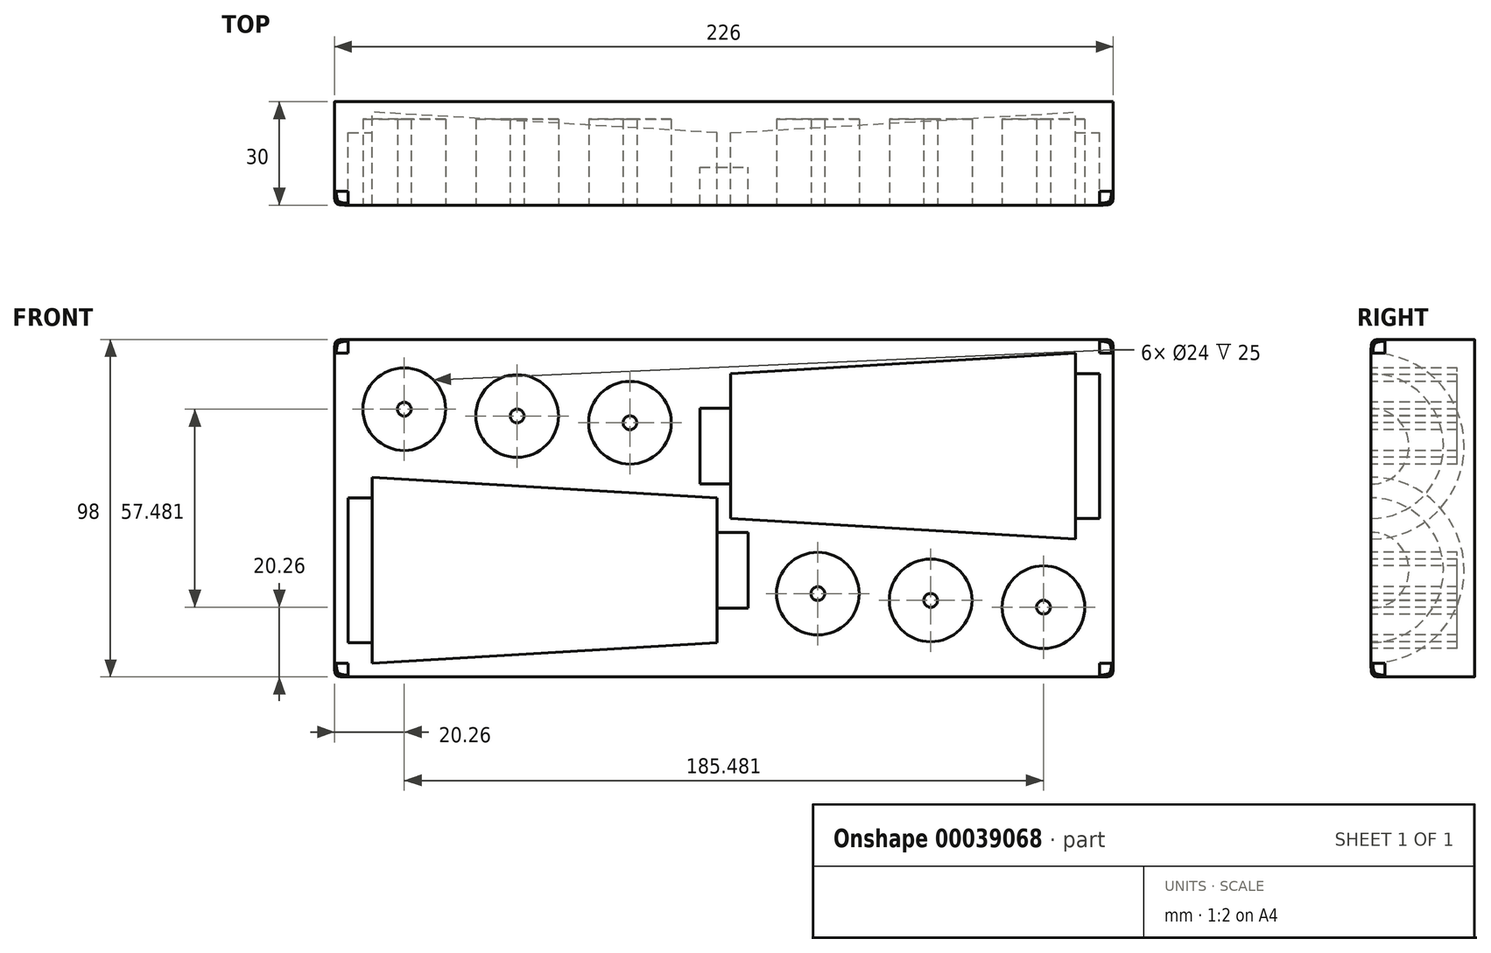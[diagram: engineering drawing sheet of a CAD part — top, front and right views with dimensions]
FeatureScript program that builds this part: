
annotation { "Feature Type Name" : "Feature", "Feature Type Description" : "" }
export const myFeature = defineFeature(function(context is Context, id is Id, definition is map)
    precondition{}
    {
        {
            var Q0;
            Q0=qCreatedBy(makeId("Front.planeOp"),FACE);
            var sketch = newSketch(context, id + "F0", { "sketchPlane" : qUnion([Q0])});
            skLineSegment(sketch, "E0.rect.bottom", {"start": v(-113, -49) * mm, "end": v(113, -49) * mm});
            skLineSegment(sketch, "E0.rect.top", {"start": v(-113, 49) * mm, "end": v(113, 49) * mm});
            skLineSegment(sketch, "E0.rect.left", {"start": v(-113, -49) * mm, "end": v(-113, 49) * mm});
            skLineSegment(sketch, "E0.rect.right", {"start": v(113, -49) * mm, "end": v(113, 49) * mm});
            skPoint(sketch, "E0.rect.middle", {"position": v(0, 0) * mm});
            skLineSegment(sketch, "E1", {"start": v(102, 45) * mm, "end": v(102, 39) * mm, "construction": true});
            skLineSegment(sketch, "E2", {"start": v(102, 39) * mm, "end": v(109, 39) * mm, "construction": true});
            skLineSegment(sketch, "E3", {"start": v(109, 18) * mm, "end": v(109, -3) * mm});
            skLineSegment(sketch, "E4", {"start": v(109, -3) * mm, "end": v(102, -3) * mm});
            skLineSegment(sketch, "E5", {"start": v(102, -3) * mm, "end": v(102, -9) * mm});
            skLineSegment(sketch, "E6", {"start": v(102, -9) * mm, "end": v(2, -3) * mm});
            skLineSegment(sketch, "E7", {"start": v(2, -3) * mm, "end": v(2, 7) * mm});
            skLineSegment(sketch, "E8", {"start": v(2, 7) * mm, "end": v(-7, 7) * mm});
            skLineSegment(sketch, "E9", {"start": v(-7, 7) * mm, "end": v(-7, 18) * mm});
            skLineSegment(sketch, "E10", {"start": v(-7, 29) * mm, "end": v(2, 29) * mm, "construction": true});
            skLineSegment(sketch, "E11", {"start": v(2, 29) * mm, "end": v(2, 39) * mm, "construction": true});
            skLineSegment(sketch, "E12", {"start": v(2, 39) * mm, "end": v(102, 45) * mm, "construction": true});
            skLineSegment(sketch, "E13", {"start": v(-7, 18) * mm, "end": v(109, 18) * mm});
            skLineSegment(sketch, "E14", {"start": v(51.88, -8) * mm, "end": v(113, -11.66) * mm, "construction": true});
            skLineSegment(sketch, "E15", {"start": v(52, -6) * mm, "end": v(51.88, -8) * mm, "construction": true});
            skLineSegment(sketch, "E16", {"start": v(-102, 9) * mm, "end": v(-2, 3) * mm, "construction": true});
            skLineSegment(sketch, "E17", {"start": v(-2, 3) * mm, "end": v(-2, -7) * mm, "construction": true});
            skLineSegment(sketch, "E18", {"start": v(-2, -7) * mm, "end": v(7, -7) * mm, "construction": true});
            skLineSegment(sketch, "E19", {"start": v(7, -18) * mm, "end": v(7, -29) * mm});
            skLineSegment(sketch, "E20", {"start": v(7, -29) * mm, "end": v(-2, -29) * mm});
            skLineSegment(sketch, "E21", {"start": v(-2, -29) * mm, "end": v(-2, -39) * mm});
            skLineSegment(sketch, "E22", {"start": v(-2, -39) * mm, "end": v(-102, -45) * mm});
            skLineSegment(sketch, "E23", {"start": v(-102, -45) * mm, "end": v(-102, -39) * mm});
            skLineSegment(sketch, "E24", {"start": v(-102, -39) * mm, "end": v(-109, -39) * mm});
            skLineSegment(sketch, "E25", {"start": v(-109, -39) * mm, "end": v(-109, -18) * mm});
            skLineSegment(sketch, "E26", {"start": v(-109, 3) * mm, "end": v(-102, 3) * mm, "construction": true});
            skLineSegment(sketch, "E27", {"start": v(-102, 3) * mm, "end": v(-102, 9) * mm, "construction": true});
            skLineSegment(sketch, "E28", {"start": v(-109, -18) * mm, "end": v(7, -18) * mm});
            skPoint(sketch, "E29.rect.middle", {"position": v(-57.95, 29) * mm});
            skPoint(sketch, "E30.rect.middle", {"position": v(57.95, -29) * mm});
            skLineSegment(sketch, "E31", {"start": v(-109, 3) * mm, "end": v(-109, -18) * mm, "construction": true});
            skLineSegment(sketch, "E32", {"start": v(-7, 29) * mm, "end": v(-7, 18) * mm, "construction": true});
            skLineSegment(sketch, "E33", {"start": v(109, 39) * mm, "end": v(109, 18) * mm, "construction": true});
            skLineSegment(sketch, "E34", {"start": v(7, -7) * mm, "end": v(7, -18) * mm, "construction": true});
            skPoint(sketch, "E35.start.orphan", {"position": v(-31.95, 41) * mm});
            skPoint(sketch, "E29.rect.left.end.orphan", {"position": v(-31.95, 29) * mm});
            skPoint(sketch, "E29.rect.bottom.start.orphan", {"position": v(-31.95, 17) * mm});
            skPoint(sketch, "E29.rect.right.start.orphan", {"position": v(-83.95, 17) * mm});
            skPoint(sketch, "E36.start.orphan", {"position": v(-83.95, 41) * mm});
            skPoint(sketch, "E37.start.orphan", {"position": v(-83.95, 29) * mm});
            skPoint(sketch, "E38.end.orphan", {"position": v(31.95, -29) * mm});
            skPoint(sketch, "E30.rect.bottom.end.orphan", {"position": v(31.95, -17) * mm});
            skPoint(sketch, "E39.start.orphan", {"position": v(83.95, -17) * mm});
            skPoint(sketch, "E40.end.orphan", {"position": v(83.95, -29) * mm});
            skPoint(sketch, "E30.rect.top.end.orphan", {"position": v(31.95, -41) * mm});
            skPoint(sketch, "E30.rect.top.start.orphan", {"position": v(83.95, -41) * mm});
            skLineSegment(sketch, "E41", {"start": v(-92.74, 28.74) * mm, "end": v(-27.26, 24.81) * mm, "construction": true});
            skCircle(sketch, "E42", {"center": v(-92.74, 28.74) * mm, "radius": 12 * mm});
            skCircle(sketch, "E43", {"center": v(-60, 26.78) * mm, "radius": 12 * mm});
            skCircle(sketch, "E44", {"center": v(-27.26, 24.81) * mm, "radius": 12 * mm});
            skLineSegment(sketch, "E45", {"start": v(-104.74, 28.74) * mm, "end": v(-113, 28.74) * mm, "construction": true});
            skLineSegment(sketch, "E46", {"start": v(-92.74, 40.74) * mm, "end": v(-92.74, 49) * mm, "construction": true});
            skLineSegment(sketch, "E47", {"start": v(-15.26, 24.81) * mm, "end": v(-7, 24.81) * mm, "construction": true});
            skLineSegment(sketch, "E48", {"start": v(-60.72, 14.8) * mm, "end": v(-61.21, 6.55) * mm, "construction": true});
            skLineSegment(sketch, "E49", {"start": v(27.26, -24.81) * mm, "end": v(92.74, -28.74) * mm, "construction": true});
            skCircle(sketch, "E50", {"center": v(92.74, -28.74) * mm, "radius": 12 * mm});
            skCircle(sketch, "E51", {"center": v(60, -26.78) * mm, "radius": 12 * mm});
            skCircle(sketch, "E52", {"center": v(27.26, -24.81) * mm, "radius": 12 * mm});
            skLineSegment(sketch, "E53", {"start": v(104.74, -28.74) * mm, "end": v(113, -28.74) * mm, "construction": true});
            skLineSegment(sketch, "E54", {"start": v(92.74, -40.74) * mm, "end": v(92.74, -49) * mm, "construction": true});
            skLineSegment(sketch, "E55", {"start": v(60.72, -14.8) * mm, "end": v(61.21, -6.55) * mm, "construction": true});
            skLineSegment(sketch, "E56", {"start": v(15.26, -24.81) * mm, "end": v(7, -24.81) * mm, "construction": true});
            skCircle(sketch, "E57", {"center": v(-92.74, 28.74) * mm, "radius": 2 * mm});
            skCircle(sketch, "E58", {"center": v(-60, 26.78) * mm, "radius": 2 * mm});
            skCircle(sketch, "E59", {"center": v(-27.26, 24.81) * mm, "radius": 2 * mm});
            skCircle(sketch, "E60", {"center": v(27.26, -24.81) * mm, "radius": 2 * mm});
            skCircle(sketch, "E61", {"center": v(60, -26.78) * mm, "radius": 2 * mm});
            skCircle(sketch, "E62", {"center": v(92.74, -28.74) * mm, "radius": 2 * mm});
            skSolve(sketch);
        }
        {
            var Q0;
            Q0=makeQuery(id+"F0.imprint","IMPRINT",FACE,{"disambiguationData":[TD([[makeQuery(id+"F0.imprint","IMPRINT",EDGE,{"derivedFrom":sQuery(id+"F0.wireOp",EDGE,"E19")}),-1.0]])]});
            var Q1;
            Q1=makeQuery(id+"F0.imprint","IMPRINT",FACE,{"disambiguationData":[TD([[makeQuery(id+"F0.imprint","IMPRINT",EDGE,{"derivedFrom":sQuery(id+"F0.wireOp",EDGE,"E3")}),-1.0]])]});
            var Q2;
            Q2=makeQuery(id+"F0.imprint","IMPRINT",FACE,{"disambiguationData":[TD([[makeQuery(id+"F0.imprint","IMPRINT",EDGE,{"derivedFrom":sQuery(id+"F0.wireOp",EDGE,"E42")}),1.0]])]});
            var Q3;
            Q3=makeQuery(id+"F0.imprint","IMPRINT",FACE,{"disambiguationData":[TD([[makeQuery(id+"F0.imprint","IMPRINT",EDGE,{"derivedFrom":sQuery(id+"F0.wireOp",EDGE,"E43")}),1.0]])]});
            var Q4;
            Q4=makeQuery(id+"F0.imprint","IMPRINT",FACE,{"disambiguationData":[TD([[makeQuery(id+"F0.imprint","IMPRINT",EDGE,{"derivedFrom":sQuery(id+"F0.wireOp",EDGE,"E44")}),1.0]])]});
            var Q5;
            Q5=makeQuery(id+"F0.imprint","IMPRINT",FACE,{"disambiguationData":[TD([[makeQuery(id+"F0.imprint","IMPRINT",EDGE,{"derivedFrom":sQuery(id+"F0.wireOp",EDGE,"E52")}),1.0]])]});
            var Q6;
            Q6=makeQuery(id+"F0.imprint","IMPRINT",FACE,{"disambiguationData":[TD([[makeQuery(id+"F0.imprint","IMPRINT",EDGE,{"derivedFrom":sQuery(id+"F0.wireOp",EDGE,"E51")}),1.0]])]});
            var Q7;
            Q7=makeQuery(id+"F0.imprint","IMPRINT",FACE,{"disambiguationData":[TD([[makeQuery(id+"F0.imprint","IMPRINT",EDGE,{"derivedFrom":sQuery(id+"F0.wireOp",EDGE,"E60")}),1.0]])]});
            var Q8;
            Q8=makeQuery(id+"F0.imprint","IMPRINT",FACE,{"disambiguationData":[TD([[makeQuery(id+"F0.imprint","IMPRINT",EDGE,{"derivedFrom":sQuery(id+"F0.wireOp",EDGE,"E61")}),1.0]])]});
            var Q9;
            Q9=makeQuery(id+"F0.imprint","IMPRINT",FACE,{"disambiguationData":[TD([[makeQuery(id+"F0.imprint","IMPRINT",EDGE,{"derivedFrom":sQuery(id+"F0.wireOp",EDGE,"E50")}),1.0]])]});
            var Q10;
            Q10=makeQuery(id+"F0.imprint","IMPRINT",FACE,{"disambiguationData":[TD([[makeQuery(id+"F0.imprint","IMPRINT",EDGE,{"derivedFrom":sQuery(id+"F0.wireOp",EDGE,"E62")}),1.0]])]});
            var Q11;
            Q11=makeQuery(id+"F0.imprint","IMPRINT",FACE,{"disambiguationData":[TD([[makeQuery(id+"F0.imprint","IMPRINT",EDGE,{"derivedFrom":sQuery(id+"F0.wireOp",EDGE,"E57")}),1.0]])]});
            var Q12;
            Q12=makeQuery(id+"F0.imprint","IMPRINT",FACE,{"disambiguationData":[TD([[makeQuery(id+"F0.imprint","IMPRINT",EDGE,{"derivedFrom":sQuery(id+"F0.wireOp",EDGE,"E58")}),1.0]])]});
            var Q13;
            Q13=makeQuery(id+"F0.imprint","IMPRINT",FACE,{"disambiguationData":[TD([[makeQuery(id+"F0.imprint","IMPRINT",EDGE,{"derivedFrom":sQuery(id+"F0.wireOp",EDGE,"E59")}),1.0]])]});
            var Q14;
            Q14=makeQuery(id+"F0.imprint","IMPRINT",FACE,{"disambiguationData":[TD([[makeQuery(id+"F0.imprint","IMPRINT",EDGE,{"derivedFrom":sQuery(id+"F0.wireOp",EDGE,"E0.rect.bottom")}),1.0]])]});
            extrude(context, id + "F1", {"entities" : qUnion([Q0, Q1, Q2, Q3, Q4, Q5, Q6, Q7, Q8, Q9, Q10, Q11, Q12, Q13, Q14]), "oppositeDirection" : true, "depth" : 30 * mm});
        }
        {
            var Q0;
            Q0=makeQuery(id+"F0.imprint","IMPRINT",FACE,{"disambiguationData":[TD([[makeQuery(id+"F0.imprint","IMPRINT",EDGE,{"derivedFrom":sQuery(id+"F0.wireOp",EDGE,"E3")}),-1.0]])]});
            var Q1;
            Q1=sQuery(id+"F0.wireOp",EDGE,"E13");
            revolve(context, id + "F2", {"operationType" : NewBodyOperationType.REMOVE, "entities" : qUnion([Q0]), "axis" : qUnion([Q1]), "revolveType" : RevolveType.FULL, "oppositeDirection" : true});
        }
        {
            var Q0;
            Q0=makeQuery(id+"F0.imprint","IMPRINT",FACE,{"disambiguationData":[TD([[makeQuery(id+"F0.imprint","IMPRINT",EDGE,{"derivedFrom":sQuery(id+"F0.wireOp",EDGE,"E19")}),-1.0]])]});
            var Q1;
            Q1=sQuery(id+"F0.wireOp",EDGE,"E28");
            revolve(context, id + "F3", {"operationType" : NewBodyOperationType.REMOVE, "entities" : qUnion([Q0]), "axis" : qUnion([Q1]), "revolveType" : RevolveType.FULL, "oppositeDirection" : true});
        }
        {
            var Q0;
            Q0=makeQuery(id+"F0.imprint","IMPRINT",FACE,{"disambiguationData":[TD([[makeQuery(id+"F0.imprint","IMPRINT",EDGE,{"derivedFrom":sQuery(id+"F0.wireOp",EDGE,"E42")}),1.0]])]});
            var Q1;
            Q1=makeQuery(id+"F0.imprint","IMPRINT",FACE,{"disambiguationData":[TD([[makeQuery(id+"F0.imprint","IMPRINT",EDGE,{"derivedFrom":sQuery(id+"F0.wireOp",EDGE,"E43")}),1.0]])]});
            var Q2;
            Q2=makeQuery(id+"F0.imprint","IMPRINT",FACE,{"disambiguationData":[TD([[makeQuery(id+"F0.imprint","IMPRINT",EDGE,{"derivedFrom":sQuery(id+"F0.wireOp",EDGE,"E44")}),1.0]])]});
            var Q3;
            Q3=makeQuery(id+"F0.imprint","IMPRINT",FACE,{"disambiguationData":[TD([[makeQuery(id+"F0.imprint","IMPRINT",EDGE,{"derivedFrom":sQuery(id+"F0.wireOp",EDGE,"E52")}),1.0]])]});
            var Q4;
            Q4=makeQuery(id+"F0.imprint","IMPRINT",FACE,{"disambiguationData":[TD([[makeQuery(id+"F0.imprint","IMPRINT",EDGE,{"derivedFrom":sQuery(id+"F0.wireOp",EDGE,"E51")}),1.0]])]});
            var Q5;
            Q5=makeQuery(id+"F0.imprint","IMPRINT",FACE,{"disambiguationData":[TD([[makeQuery(id+"F0.imprint","IMPRINT",EDGE,{"derivedFrom":sQuery(id+"F0.wireOp",EDGE,"E50")}),1.0]])]});
            extrude(context, id + "F4", {"entities" : qUnion([Q0, Q1, Q2, Q3, Q4, Q5]), "operationType" : NewBodyOperationType.REMOVE, "oppositeDirection" : true, "depth" : 25 * mm});
        }
        {
            var Q0;
            Q0=makeQuery(id+"F1.opExtrude","SWEPT_EDGE",EDGE,{"disambiguationData":[OSD([sQuery(id+"F0.wireOp",EDGE,"E0.rect.bottom"),sQuery(id+"F0.wireOp",EDGE,"E0.rect.left")])]});
            var Q1;
            Q1=makeQuery(id+"F1.opExtrude","SWEPT_EDGE",EDGE,{"disambiguationData":[OSD([sQuery(id+"F0.wireOp",EDGE,"E0.rect.top"),sQuery(id+"F0.wireOp",EDGE,"E0.rect.left")])]});
            var Q2;
            Q2=makeQuery(id+"F1.opExtrude","SWEPT_EDGE",EDGE,{"disambiguationData":[OSD([sQuery(id+"F0.wireOp",EDGE,"E0.rect.bottom"),sQuery(id+"F0.wireOp",EDGE,"E0.rect.right")])]});
            var Q3;
            Q3=makeQuery(id+"F1.opExtrude","SWEPT_EDGE",EDGE,{"disambiguationData":[OSD([sQuery(id+"F0.wireOp",EDGE,"E0.rect.top"),sQuery(id+"F0.wireOp",EDGE,"E0.rect.right")])]});
            var Q4;
            Q4=makeQuery(id+"F1.opExtrude","CAP_EDGE",EDGE,{"disambiguationData":[OSD([sQuery(id+"F0.wireOp",EDGE,"E0.rect.right")])],"isStart":true});
            var Q5;
            Q5=makeQuery(id+"F1.opExtrude","CAP_EDGE",EDGE,{"disambiguationData":[OSD([sQuery(id+"F0.wireOp",EDGE,"E0.rect.bottom")])],"isStart":true});
            var Q6;
            Q6=makeQuery(id+"F1.opExtrude","CAP_EDGE",EDGE,{"disambiguationData":[OSD([sQuery(id+"F0.wireOp",EDGE,"E0.rect.top")])],"isStart":true});
            var Q7;
            Q7=makeQuery(id+"F1.opExtrude","CAP_EDGE",EDGE,{"disambiguationData":[OSD([sQuery(id+"F0.wireOp",EDGE,"E0.rect.left")])],"isStart":true});
            var Q8;
            Q8=makeQuery(id+"F4.boolean.opBoolean","COPY",EDGE,{"derivedFrom":makeQuery(id+"F4.opExtrude","CAP_EDGE",EDGE,{"disambiguationData":[OSD([sQuery(id+"F0.wireOp",EDGE,"E42")])],"isStart":true})});
            var Q9;
            Q9=makeQuery(id+"F4.boolean.opBoolean","COPY",EDGE,{"derivedFrom":makeQuery(id+"F4.opExtrude","CAP_EDGE",EDGE,{"disambiguationData":[OSD([sQuery(id+"F0.wireOp",EDGE,"E43")])],"isStart":true})});
            var Q10;
            Q10=makeQuery(id+"F4.boolean.opBoolean","COPY",EDGE,{"derivedFrom":makeQuery(id+"F4.opExtrude","CAP_EDGE",EDGE,{"disambiguationData":[OSD([sQuery(id+"F0.wireOp",EDGE,"E44")])],"isStart":true})});
            var Q11;
            Q11=makeQuery(id+"F4.boolean.opBoolean","COPY",EDGE,{"derivedFrom":makeQuery(id+"F4.opExtrude","CAP_EDGE",EDGE,{"disambiguationData":[OSD([sQuery(id+"F0.wireOp",EDGE,"E52")])],"isStart":true})});
            var Q12;
            Q12=makeQuery(id+"F4.boolean.opBoolean","COPY",EDGE,{"derivedFrom":makeQuery(id+"F4.opExtrude","CAP_EDGE",EDGE,{"disambiguationData":[OSD([sQuery(id+"F0.wireOp",EDGE,"E51")])],"isStart":true})});
            var Q13;
            Q13=makeQuery(id+"F4.boolean.opBoolean","COPY",EDGE,{"derivedFrom":makeQuery(id+"F4.opExtrude","CAP_EDGE",EDGE,{"disambiguationData":[OSD([sQuery(id+"F0.wireOp",EDGE,"E50")])],"isStart":true})});
            fillet(context, id + "F5", {"entities" : qUnion([Q0, Q1, Q2, Q3, Q4, Q5, Q6, Q7, Q8, Q9, Q10, Q11, Q12, Q13]), "radius" : 4 * mm, "tangentPropagation" : true, "rho" : 0.74, "crossSection" : FilletCrossSection.CONIC, "allowEdgeOverflow" : false});
        }
    });
